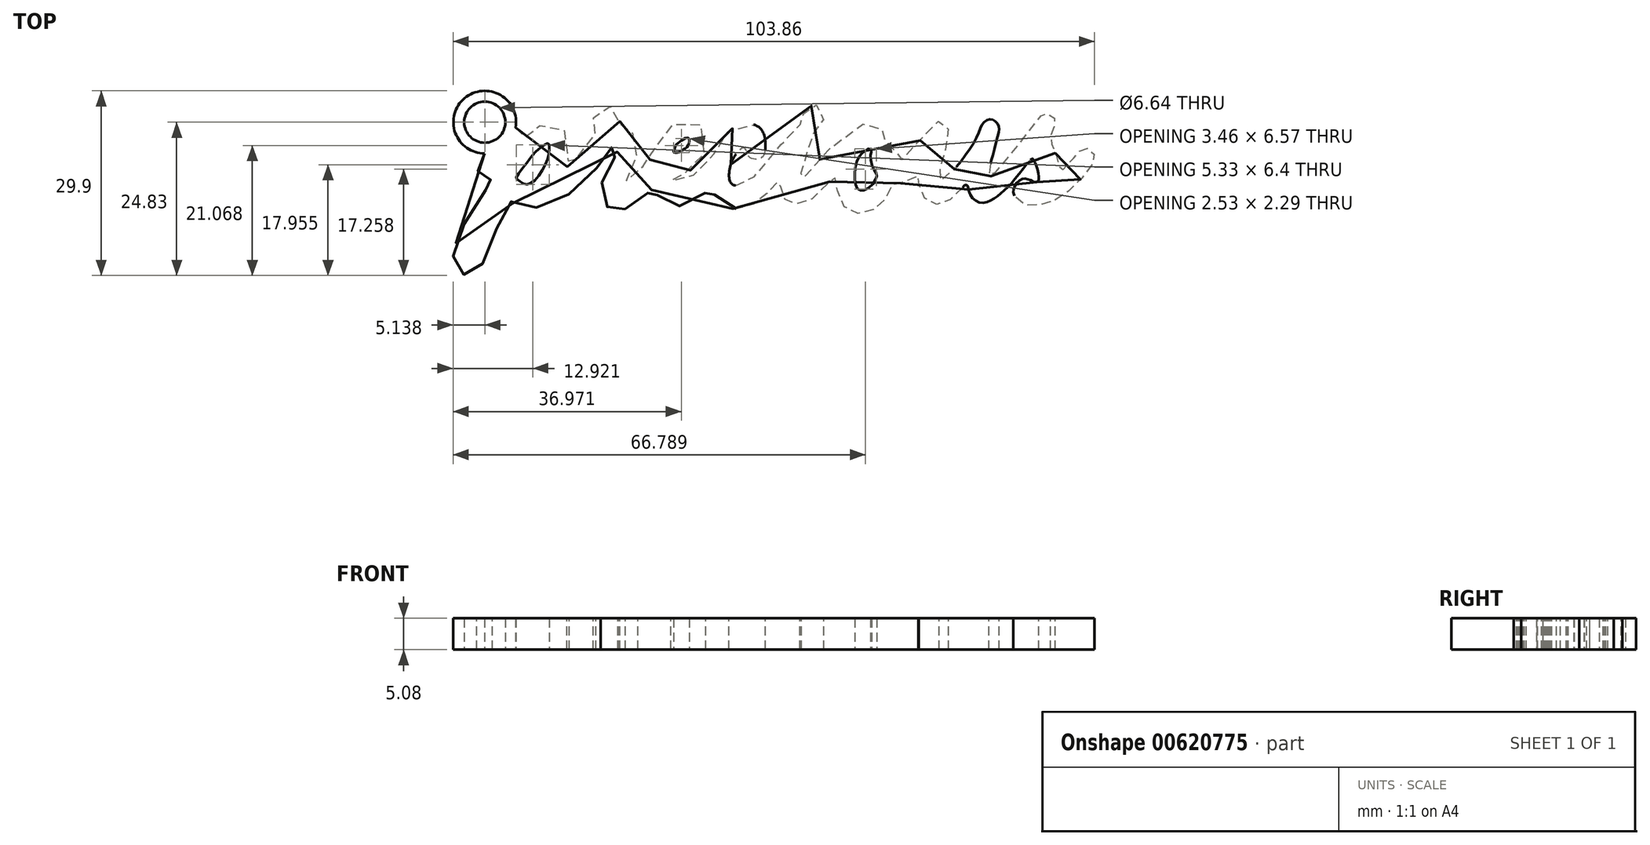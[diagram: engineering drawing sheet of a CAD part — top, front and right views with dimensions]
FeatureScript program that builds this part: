
annotation { "Feature Type Name" : "Feature", "Feature Type Description" : "" }
export const myFeature = defineFeature(function(context is Context, id is Id, definition is map)
    precondition{}
    {
        {
            var Q0;
            Q0=qCreatedBy(makeId("Top.planeOp"),FACE);
            var sketch = newSketch(context, id + "F0", { "sketchPlane" : qUnion([Q0])});
            skPoint(sketch, "E0.middle", {"position": v(0, 0) * mm});
            skFitSpline(sketch, "E1", {"points": [v(26.19, 8.06) * mm, v(25.57, 7.69) * mm, v(24.76, 6.94) * mm, v(24.07, 5.2) * mm, v(23.95, 3.26) * mm, v(24.2, 1.9) * mm, v(24.63, 1.4) * mm, v(25.32, 1.33) * mm, v(26.69, 2.2) * mm, v(27.44, 3.39) * mm, v(27.5, 3.82) * mm, v(27.31, 4.2) * mm, v(26.69, 5.38) * mm, v(26.5, 6.94) * mm, v(26.63, 7.62) * mm, v(26.63, 8) * mm, v(26.19, 8.06) * mm]});
            skFitSpline(sketch, "E2", {"points": [v(-4.4, 9.17) * mm, v(-3.68, 9.66) * mm, v(-3.1, 9.82) * mm, v(-2.87, 9.58) * mm, v(-2.95, 8.93) * mm, v(-3.27, 8.28) * mm, v(-4.16, 7.72) * mm, v(-4.8, 7.4) * mm, v(-5.37, 7.47) * mm, v(-5.37, 7.72) * mm, v(-5.05, 8.6) * mm, v(-4.4, 9.17) * mm]});
            skFitSpline(sketch, "E3", {"points": [v(-28.3, 6.88) * mm, v(-27.05, 8.19) * mm, v(-26.11, 8.8) * mm, v(-25.74, 8.93) * mm, v(-25.55, 8.75) * mm, v(-25.55, 7.81) * mm, v(-25.74, 6.63) * mm, v(-26.43, 4.95) * mm, v(-27.61, 3.2) * mm, v(-28.67, 2.4) * mm, v(-29.3, 2.27) * mm, v(-29.98, 2.58) * mm, v(-30.66, 3.08) * mm, v(-30.91, 3.33) * mm, v(-30.85, 3.51) * mm, v(-29.73, 5.07) * mm, v(-28.8, 6.25) * mm, v(-28.3, 6.88) * mm]});
            skPoint(sketch, "E4.167.internal.snap0", {"position": v(65.33, 1.48) * mm});
            skPoint(sketch, "E4.213.internal.snap0", {"position": v(65.33, 1.48) * mm});
            skPoint(sketch, "E4.214.internal.snap0", {"position": v(65.33, 1.48) * mm});
            skFitSpline(sketch, "E4", {"points": [v(-28.75, 10.55) * mm, v(-27.28, 11.7) * mm, v(-25.18, 12.12) * mm, v(-23.4, 11.38) * mm, v(-22.35, 9.08) * mm, v(-22.46, 6.14) * mm, v(-22.63, 5.29) * mm, v(-22.63, 5.14) * mm, v(-22.49, 5.2) * mm, v(-21.31, 6.31) * mm, v(-19, 9.03) * mm, v(-18.02, 10.52) * mm, v(-17.98, 10.74) * mm, v(-18.2, 11.33) * mm, v(-18.43, 12.48) * mm, v(-18.17, 13.7) * mm, v(-17.26, 14.63) * mm, v(-15.76, 14.94) * mm, v(-14.64, 14.26) * mm, v(-14.14, 12.83) * mm, v(-14.14, 12.08) * mm, v(-14.14, 11.9) * mm, v(-13.96, 11.77) * mm, v(-12.77, 11.14) * mm, v(-11.84, 10.27) * mm, v(-11.22, 8.59) * mm, v(-11.4, 6.84) * mm, v(-12.21, 4.66) * mm, v(-13.02, 2.98) * mm, v(-13.2, 2.67) * mm, v(-13.2, 2.66) * mm, v(-13.14, 2.63) * mm, v(-12.58, 2.99) * mm, v(-9.32, 6.2) * mm, v(-9, 6.45) * mm, v(-8.63, 7.32) * mm, v(-8.14, 8.94) * mm, v(-6.45, 11.25) * mm, v(-3.46, 12.8) * mm, v(-1.4, 12.3) * mm, v(-0.35, 10.56) * mm, v(-0.35, 7.72) * mm, v(-1.4, 5.58) * mm, v(-3.4, 4.14) * mm, v(-5.02, 3.58) * mm, v(-5.83, 3.33) * mm, v(-5.83, 3.2) * mm, v(-5.7, 2.96) * mm, v(-5.37, 2.52) * mm, v(-3.77, 2.83) * mm, v(-1.22, 4.58) * mm, v(0.84, 6.82) * mm, v(1.27, 7.38) * mm, v(2.08, 9.06) * mm, v(3.45, 10.87) * mm, v(5.8, 12) * mm, v(7.6, 11.94) * mm, v(9.03, 10.82) * mm, v(9.4, 7.72) * mm, v(8.78, 6.52) * mm, v(7.47, 6.4) * mm, v(6.66, 6.96) * mm, v(6.23, 8.02) * mm, v(5.92, 8.2) * mm, v(5.37, 7.9) * mm, v(4.34, 6.61) * mm, v(3.62, 4.38) * mm, v(3.74, 2.7) * mm, v(4.4, 2.14) * mm, v(5.85, 2.34) * mm, v(9.08, 5) * mm, v(14.65, 11.82) * mm, v(15.18, 12.03) * mm, v(15.28, 12.14) * mm, v(15.28, 12.77) * mm, v(15.91, 14.13) * mm, v(17.06, 15.07) * mm, v(18.11, 15.07) * mm, v(18.95, 13.6) * mm, v(18.11, 11.4) * mm, v(17.38, 10.67) * mm, v(17.06, 10.35) * mm, v(16.85, 9.52) * mm, v(15.28, 4.8) * mm, v(15.18, 3.82) * mm, v(15.07, 3.23) * mm, v(15.28, 3.12) * mm, v(16.12, 3.82) * mm, v(23.14, 10.98) * mm, v(27.5, 12.14) * mm, v(28.38, 10.88) * mm, v(28.49, 9.73) * mm, v(28.7, 9.41) * mm, v(29.12, 9.41) * mm, v(30.27, 8.36) * mm, v(30.9, 6.37) * mm, v(31, 6.16) * mm, v(31.32, 6.16) * mm, v(34.98, 9.94) * mm, v(36.77, 12.24) * mm, v(38.02, 12.45) * mm, v(38.8, 11.94) * mm, v(39.11, 10.76) * mm, v(38.74, 8.4) * mm, v(38, 5.71) * mm, v(37.62, 4.47) * mm, v(37.62, 3.47) * mm, v(37.8, 2.9) * mm, v(38.12, 2.9) * mm, v(40.55, 5.34) * mm, v(43.79, 10.14) * mm, v(44.66, 12.13) * mm, v(45.72, 12.82) * mm, v(46.65, 12.5) * mm, v(47.28, 11.57) * mm, v(47.15, 10.45) * mm, v(46.1, 6.33) * mm, v(45.78, 5.03) * mm, v(45.72, 3.82) * mm, v(45.9, 3.6) * mm, v(46.34, 3.82) * mm, v(54.08, 13.4) * mm, v(54.33, 13.7) * mm, v(54.82, 13.77) * mm, v(55.57, 13.65) * mm, v(56.26, 13.02) * mm, v(56.38, 12.03) * mm, v(56.2, 11.53) * mm, v(55.82, 10.78) * mm, v(55.64, 10.03) * mm, v(55.7, 9.28) * mm, v(56.07, 8.04) * mm, v(56.7, 6.54) * mm, v(57, 5.36) * mm, v(57.26, 4.61) * mm, v(57.44, 4.55) * mm, v(57.88, 4.92) * mm, v(59.6, 6.8) * mm, v(60.05, 7.39) * mm, v(60.6, 7.95) * mm, v(61.27, 8.17) * mm, v(62.08, 7.9) * mm, v(62.6, 7.28) * mm, v(62.75, 6.65) * mm, v(62.45, 5.61) * mm, v(60.05, 2.6) * mm, v(57.79, 0.6) * mm, v(55.41, -0.69) * mm, v(53.3, -1.13) * mm, v(51, -0.91) * mm, v(49.67, 0.68) * mm, v(49.93, 2.16) * mm, v(51.04, 3.13) * mm, v(52.08, 3.1) * mm, v(52.78, 2.76) * mm, v(53.27, 2.65) * mm, v(53.64, 2.83) * mm, v(53.7, 3.82) * mm, v(53.2, 5.61) * mm, v(52.82, 6.31) * mm, v(52.7, 6.43) * mm, v(52.52, 6.39) * mm, v(49.93, 3.2) * mm, v(47.63, 0.87) * mm, v(45.78, -0.4) * mm, v(43.94, -0.59) * mm, v(42.57, 0.67) * mm, v(42.36, 1.48) * mm, v(42.16, 2.1) * mm, v(41.8, 2.17) * mm, v(41.38, 1.72) * mm, v(39.12, -0.39) * mm, v(37.3, -0.95) * mm, v(35.57, -0.28) * mm, v(34.64, 1.17) * mm, v(34.23, 3.2) * mm, v(34.27, 3.54) * mm, v(34.12, 3.69) * mm, v(33.82, 3.69) * mm, v(33, 3.1) * mm, v(31.27, 2.46) * mm, v(30.34, 2.39) * mm, v(30.12, 2.39) * mm, v(30, 2.2) * mm, v(28.71, -0.35) * mm, v(27, -1.8) * mm, v(24.63, -2.4) * mm, v(22.43, -1.6) * mm, v(21.19, 1.02) * mm, v(20.81, 3.14) * mm, v(20.75, 3.39) * mm, v(20.56, 3.45) * mm, v(20.25, 3.14) * mm, v(16.39, -0.48) * mm, v(14.08, -0.85) * mm, v(12.9, -0.35) * mm, v(12.03, 0.96) * mm, v(11.84, 2.64) * mm, v(11.6, 2.83) * mm, v(11.34, 2.58) * mm, v(9.53, 0.65) * mm, v(7.35, -1.04) * mm, v(4.24, -1.66) * mm, v(1.87, -0.54) * mm, v(1.12, 0.9) * mm, v(0.93, 1.4) * mm, v(0.69, 1.4) * mm, v(0.25, 1.4) * mm, v(-0.62, 0.58) * mm, v(-3.02, -0.9) * mm, v(-5.37, -1.23) * mm, v(-7.3, -0.5) * mm, v(-8.3, 1.13) * mm, v(-8.5, 1.48) * mm, v(-8.62, 1.48) * mm, v(-8.96, 1.4) * mm, v(-9.73, 0.76) * mm, v(-11.79, -0.84) * mm, v(-13.53, -1.8) * mm, v(-14.22, -1.95) * mm, v(-15.21, -1.84) * mm, v(-16.51, -0.98) * mm, v(-17.18, 1.04) * mm, v(-16.8, 3.2) * mm, v(-15.46, 5.65) * mm, v(-14.69, 7.2) * mm, v(-14.4, 7.96) * mm, v(-14.54, 8.06) * mm, v(-15.26, 8.25) * mm, v(-15.6, 8.15) * mm, v(-16.37, 6.94) * mm, v(-18.39, 4.3) * mm, v(-21.75, 1.09) * mm, v(-25.26, -0.83) * mm, v(-28.72, -1.5) * mm, v(-31.23, -0.93) * mm, v(-31.8, -0.44) * mm, v(-32.12, -0.36) * mm, v(-32.44, -0.68) * mm, v(-35.6, -9.09) * mm, v(-36.08, -10.14) * mm, v(-37.2, -11.83) * mm, v(-38.74, -12.48) * mm, v(-39.87, -12) * mm, v(-40.84, -10.78) * mm, v(-41.09, -9.17) * mm, v(-40.12, -5.85) * mm, v(-38.1, -2.14) * mm, v(-35.5, 1.9) * mm, v(-35, 2.8) * mm, v(-34.8, 3.09) * mm, v(-34.76, 3.17) * mm, v(-34.88, 3.12) * mm, v(-35.25, 3.03) * mm, v(-35.85, 3.14) * mm, v(-36.5, 3.66) * mm, v(-37.12, 4.5) * mm, v(-37.25, 5.44) * mm, v(-36.87, 6.25) * mm, v(-35.13, 8.19) * mm, v(-33.7, 9.93) * mm, v(-32.39, 11.3) * mm, v(-31.64, 11.55) * mm, v(-30.72, 11.35) * mm, v(-30.1, 10.8) * mm, v(-29.75, 10.35) * mm, v(-29.55, 10.01) * mm, v(-29.47, 9.93) * mm, v(-29.36, 9.98) * mm, v(-28.92, 10.42) * mm, v(-28.75, 10.55) * mm]});
            skArc(sketch, "E5", {"start": v(-30.98, 11.46) * mm, "mid": v(-39.23, 16.24) * mm, "end": v(-35.98, 7.28) * mm});
            skCircle(sketch, "E6", {"center": v(-35.97, 12.35) * mm, "radius": 3.32 * mm});
            skSolve(sketch);
        }
        {
            var Q0;
            Q0 = qSketchRegion(id + "F0", true);
            extrude(context, id + "F1", {"entities" : qUnion([Q0]), "depth" : 5.08 * mm, "offsetDistance" : 25.4 * mm});
        }
    });
